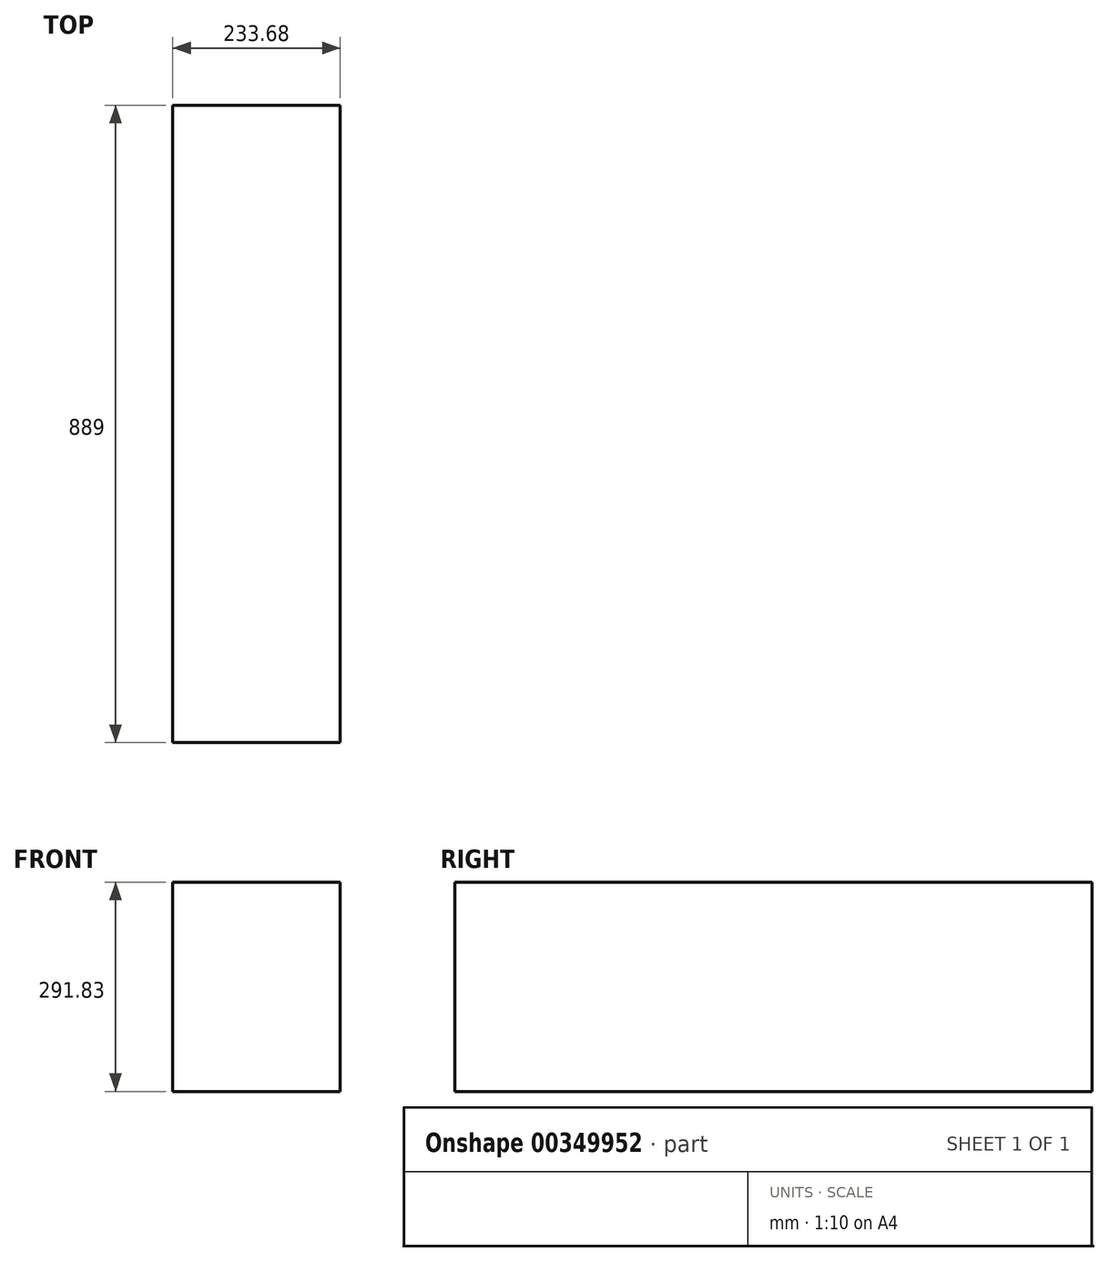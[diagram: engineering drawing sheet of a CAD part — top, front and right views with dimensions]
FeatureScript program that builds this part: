
annotation { "Feature Type Name" : "Feature", "Feature Type Description" : "" }
export const myFeature = defineFeature(function(context is Context, id is Id, definition is map)
    precondition{}
    {
        {
            var Q0;
            Q0=qCreatedBy(makeId("Front.planeOp"),FACE);
            var sketch = newSketch(context, id + "F0", { "sketchPlane" : qUnion([Q0])});
            skLineSegment(sketch, "E0.bottom", {"start": v(-129.16, 113.5) * mm, "end": v(104.52, 113.5) * mm});
            skLineSegment(sketch, "E0.top", {"start": v(-129.16, -178.33) * mm, "end": v(104.52, -178.33) * mm});
            skLineSegment(sketch, "E0.left", {"start": v(-129.16, 113.5) * mm, "end": v(-129.16, -178.33) * mm});
            skLineSegment(sketch, "E0.right", {"start": v(104.52, 113.5) * mm, "end": v(104.52, -178.33) * mm});
            skSolve(sketch);
        }
        {
            var Q0;
            Q0 = qSketchRegion(id + "F0", true);
            extrude(context, id + "F1", {"entities" : qUnion([Q0]), "depth" : 889 * mm});
        }
    });
